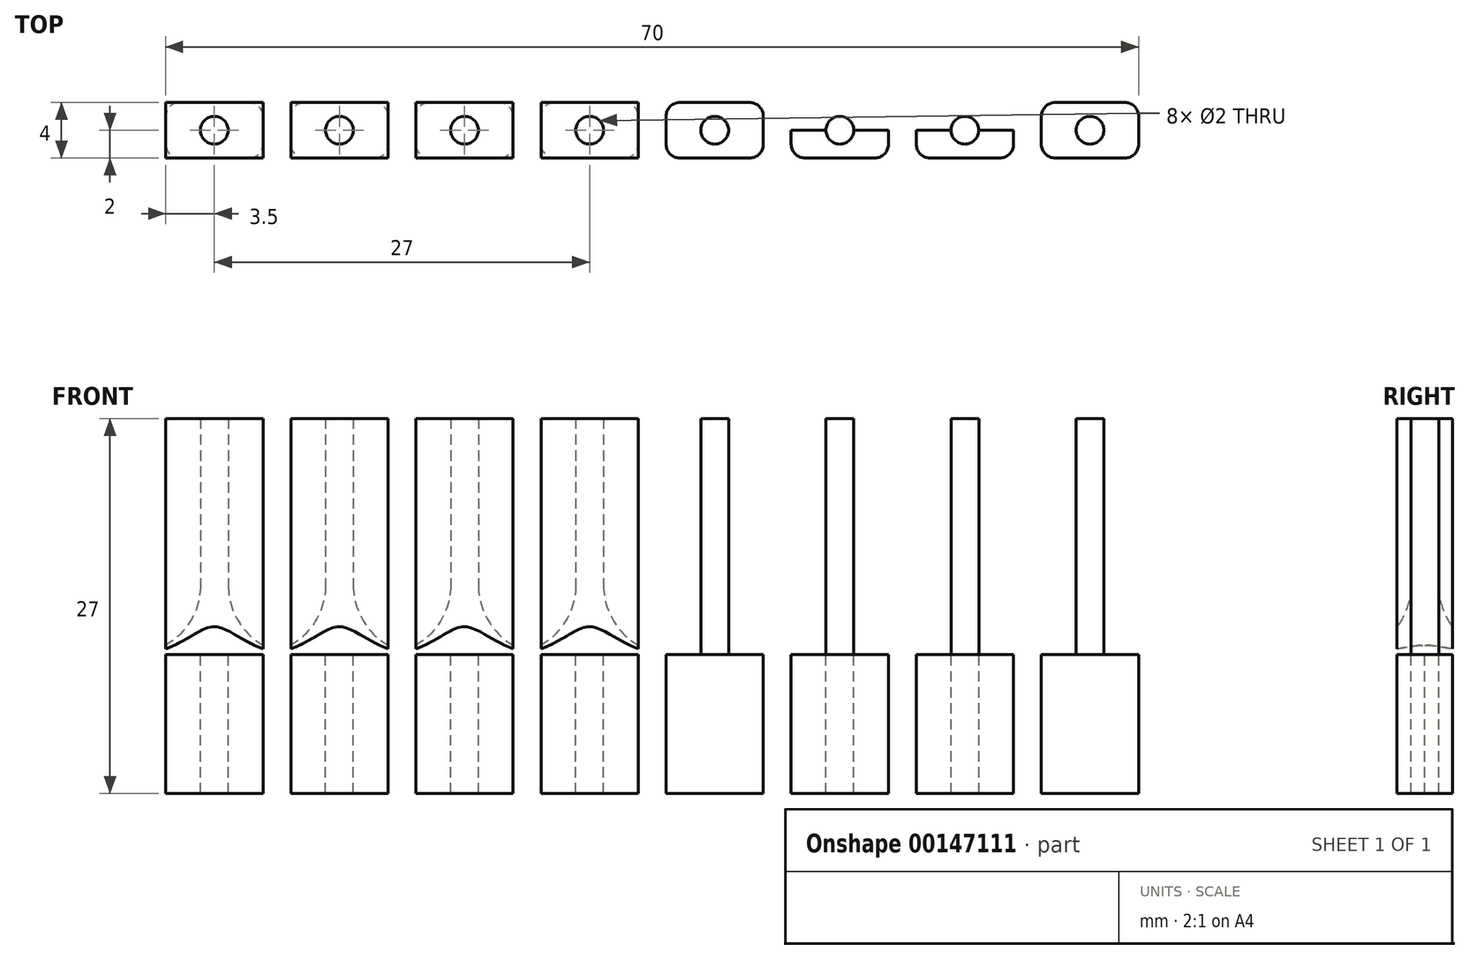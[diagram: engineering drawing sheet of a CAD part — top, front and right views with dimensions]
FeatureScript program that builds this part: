
annotation { "Feature Type Name" : "Feature", "Feature Type Description" : "" }
export const myFeature = defineFeature(function(context is Context, id is Id, definition is map)
    precondition{}
    {
        {
            var Q0;
            Q0=qCreatedBy(makeId("Top.planeOp"),FACE);
            var sketch = newSketch(context, id + "F0", { "sketchPlane" : qUnion([Q0])});
            skLineSegment(sketch, "E0.bottom", {"start": v(35, 2) * mm, "end": v(-35, 2) * mm});
            skLineSegment(sketch, "E0.top", {"start": v(35, -2) * mm, "end": v(-35, -2) * mm});
            skLineSegment(sketch, "E0.left", {"start": v(35, 2) * mm, "end": v(35, -2) * mm});
            skLineSegment(sketch, "E0.right", {"start": v(-35, 2) * mm, "end": v(-35, -2) * mm});
            skPoint(sketch, "E0.middle", {"position": v(0, 0) * mm});
            skLineSegment(sketch, "E1", {"start": v(0, 0) * mm, "end": v(4.5, 0) * mm});
            skLineSegment(sketch, "E2", {"start": v(4.5, 0) * mm, "end": v(13.5, 0) * mm});
            skLineSegment(sketch, "E3", {"start": v(13.5, 0) * mm, "end": v(22.5, 0) * mm});
            skLineSegment(sketch, "E4", {"start": v(22.5, 0) * mm, "end": v(31.5, 0) * mm});
            skCircle(sketch, "E5", {"center": v(4.5, 0) * mm, "radius": 1 * mm});
            skCircle(sketch, "E6", {"center": v(13.5, 0) * mm, "radius": 1 * mm});
            skCircle(sketch, "E7", {"center": v(22.5, 0) * mm, "radius": 1 * mm});
            skCircle(sketch, "E8", {"center": v(31.5, 0) * mm, "radius": 1 * mm});
            skLineSegment(sketch, "E9", {"start": v(0, 2) * mm, "end": v(8, 2) * mm});
            skLineSegment(sketch, "E10", {"start": v(8, 2) * mm, "end": v(10, 2) * mm});
            skLineSegment(sketch, "E11", {"start": v(10, 2) * mm, "end": v(17, 2) * mm});
            skLineSegment(sketch, "E12", {"start": v(17, 2) * mm, "end": v(19, 2) * mm});
            skLineSegment(sketch, "E13", {"start": v(19, 2) * mm, "end": v(26, 2) * mm});
            skLineSegment(sketch, "E14", {"start": v(26, 2) * mm, "end": v(28, 2) * mm});
            skLineSegment(sketch, "E15", {"start": v(8, 2) * mm, "end": v(8, 0.5) * mm});
            skLineSegment(sketch, "E16", {"start": v(8, 0.5) * mm, "end": v(10, 0.5) * mm});
            skLineSegment(sketch, "E17", {"start": v(10, 0.5) * mm, "end": v(10, 2) * mm});
            skLineSegment(sketch, "E18", {"start": v(17, 2) * mm, "end": v(17, 0.5) * mm});
            skLineSegment(sketch, "E19", {"start": v(17, 0.5) * mm, "end": v(19, 0.5) * mm});
            skLineSegment(sketch, "E20", {"start": v(19, 0.5) * mm, "end": v(19, 2) * mm});
            skLineSegment(sketch, "E21", {"start": v(26, 2) * mm, "end": v(26, 0.5) * mm});
            skLineSegment(sketch, "E22", {"start": v(26, 0.5) * mm, "end": v(28, 0.5) * mm});
            skLineSegment(sketch, "E23", {"start": v(28, 0.5) * mm, "end": v(28, 2) * mm});
            skLineSegment(sketch, "E24.MirrorCS", {"start": v(8, -0.5) * mm, "end": v(10, -0.5) * mm});
            skLineSegment(sketch, "E25.MirrorCS", {"start": v(8, -2) * mm, "end": v(8, -0.5) * mm});
            skLineSegment(sketch, "E26.MirrorCS", {"start": v(10, -0.5) * mm, "end": v(10, -2) * mm});
            skLineSegment(sketch, "E27.MirrorCS", {"start": v(17, -2) * mm, "end": v(17, -0.5) * mm});
            skLineSegment(sketch, "E28.MirrorCS", {"start": v(19, -0.5) * mm, "end": v(19, -2) * mm});
            skLineSegment(sketch, "E29.MirrorCS", {"start": v(17, -0.5) * mm, "end": v(19, -0.5) * mm});
            skLineSegment(sketch, "E30.MirrorCS", {"start": v(26, -0.5) * mm, "end": v(28, -0.5) * mm});
            skLineSegment(sketch, "E31.MirrorCS", {"start": v(28, -0.5) * mm, "end": v(28, -2) * mm});
            skLineSegment(sketch, "E32.MirrorCS", {"start": v(26, -2) * mm, "end": v(26, -0.5) * mm});
            skLineSegment(sketch, "E33", {"start": v(10, -0.5) * mm, "end": v(10, 0.5) * mm});
            skLineSegment(sketch, "E34", {"start": v(8, -0.5) * mm, "end": v(8, 0.5) * mm});
            skLineSegment(sketch, "E35", {"start": v(17, -0.5) * mm, "end": v(17, 0.5) * mm});
            skLineSegment(sketch, "E36", {"start": v(19, -0.5) * mm, "end": v(19, 0.5) * mm});
            skLineSegment(sketch, "E37", {"start": v(26, -0.5) * mm, "end": v(26, 0.5) * mm});
            skLineSegment(sketch, "E38", {"start": v(28, -0.5) * mm, "end": v(28, 0.5) * mm});
            skLineSegment(sketch, "E39.MirrorCS", {"start": v(-8, -2) * mm, "end": v(-8, -0.5) * mm});
            skCircle(sketch, "E40.MirrorC", {"center": v(-4.5, 0) * mm, "radius": 1 * mm});
            skLineSegment(sketch, "E41.MirrorCS", {"start": v(-8, 2) * mm, "end": v(-8, 0.5) * mm});
            skLineSegment(sketch, "E42.MirrorCS", {"start": v(-8, 0.5) * mm, "end": v(-10, 0.5) * mm});
            skLineSegment(sketch, "E43.MirrorCS", {"start": v(-10, -0.5) * mm, "end": v(-10, -2) * mm});
            skCircle(sketch, "E44.MirrorC", {"center": v(-13.5, 0) * mm, "radius": 1 * mm});
            skLineSegment(sketch, "E45.MirrorCS", {"start": v(-17, -2) * mm, "end": v(-17, -0.5) * mm});
            skLineSegment(sketch, "E46.MirrorCS", {"start": v(-19, -0.5) * mm, "end": v(-19, -2) * mm});
            skLineSegment(sketch, "E47.MirrorCS", {"start": v(-17, -0.5) * mm, "end": v(-19, -0.5) * mm});
            skLineSegment(sketch, "E48.MirrorCS", {"start": v(-17, 0.5) * mm, "end": v(-19, 0.5) * mm});
            skLineSegment(sketch, "E49.MirrorCS", {"start": v(-19, 0.5) * mm, "end": v(-19, 2) * mm});
            skLineSegment(sketch, "E50.MirrorCS", {"start": v(-17, 2) * mm, "end": v(-17, 0.5) * mm});
            skCircle(sketch, "E51.MirrorC", {"center": v(-22.5, 0) * mm, "radius": 1 * mm});
            skLineSegment(sketch, "E52.MirrorCS", {"start": v(-26, -2) * mm, "end": v(-26, -0.5) * mm});
            skLineSegment(sketch, "E53.MirrorCS", {"start": v(-28, -0.5) * mm, "end": v(-28, -2) * mm});
            skLineSegment(sketch, "E54.MirrorCS", {"start": v(-26, -0.5) * mm, "end": v(-28, -0.5) * mm});
            skLineSegment(sketch, "E55.MirrorCS", {"start": v(-26, 0.5) * mm, "end": v(-28, 0.5) * mm});
            skLineSegment(sketch, "E56.MirrorCS", {"start": v(-28, 0.5) * mm, "end": v(-28, 2) * mm});
            skLineSegment(sketch, "E57.MirrorCS", {"start": v(-26, 2) * mm, "end": v(-26, 0.5) * mm});
            skCircle(sketch, "E58.MirrorC", {"center": v(-31.5, 0) * mm, "radius": 1 * mm});
            skLineSegment(sketch, "E59.MirrorCS", {"start": v(-28, -0.5) * mm, "end": v(-28, 0.5) * mm});
            skLineSegment(sketch, "E60.MirrorCS", {"start": v(-26, -0.5) * mm, "end": v(-26, 0.5) * mm});
            skLineSegment(sketch, "E61.MirrorCS", {"start": v(-19, -0.5) * mm, "end": v(-19, 0.5) * mm});
            skLineSegment(sketch, "E62.MirrorCS", {"start": v(-17, -0.5) * mm, "end": v(-17, 0.5) * mm});
            skLineSegment(sketch, "E63.MirrorCS", {"start": v(-8, -0.5) * mm, "end": v(-8, 0.5) * mm});
            skLineSegment(sketch, "E64.MirrorCS", {"start": v(-10, -0.5) * mm, "end": v(-10, 0.5) * mm});
            skLineSegment(sketch, "E65.MirrorCS", {"start": v(-8, -0.5) * mm, "end": v(-10, -0.5) * mm});
            skLineSegment(sketch, "E66.MirrorCS", {"start": v(-10, 0.5) * mm, "end": v(-10, 2) * mm});
            skLineSegment(sketch, "E67", {"start": v(8, 2) * mm, "end": v(1, 2) * mm});
            skLineSegment(sketch, "E68", {"start": v(1, 2) * mm, "end": v(1, 0.5) * mm});
            skLineSegment(sketch, "E69", {"start": v(1, 0.5) * mm, "end": v(-1, 0.5) * mm});
            skLineSegment(sketch, "E70", {"start": v(-1, 0.5) * mm, "end": v(-1, 2) * mm});
            skLineSegment(sketch, "E71", {"start": v(8, -2) * mm, "end": v(1, -2) * mm});
            skLineSegment(sketch, "E72", {"start": v(1, -2) * mm, "end": v(1, -0.5) * mm});
            skLineSegment(sketch, "E73", {"start": v(1, -0.5) * mm, "end": v(-1, -0.5) * mm});
            skLineSegment(sketch, "E74", {"start": v(-1, -0.5) * mm, "end": v(-1, -2) * mm});
            skLineSegment(sketch, "E75", {"start": v(1, -0.5) * mm, "end": v(1, 0.5) * mm});
            skLineSegment(sketch, "E76", {"start": v(-1, -0.5) * mm, "end": v(-1, 0.5) * mm});
            skSolve(sketch);
        }
        {
            var Q0;
            {var subQ0=sQuery(id+"F0.wireOp",EDGE,"E0.left");Q0=makeQuery(id+"F0.imprint","IMPRINT",FACE,{"disambiguationData":[TD([[makeQuery(id+"F0.imprint","IMPRINT",EDGE,{"derivedFrom":subQ0}),-1.0]])]});}
            var Q1;
            {var subQ6=sQuery(id+"F0.wireOp",EDGE,"E0.right");Q1=makeQuery(id+"F0.imprint","IMPRINT",FACE,{"disambiguationData":[TD([[makeQuery(id+"F0.imprint","IMPRINT",EDGE,{"derivedFrom":subQ6}),1.0]])]});}
            var Q2;
            {var subQ10=sQuery(id+"F0.wireOp",EDGE,"E28.MirrorCS");Q2=makeQuery(id+"F0.imprint","IMPRINT",FACE,{"disambiguationData":[TD([[makeQuery(id+"F0.imprint","IMPRINT",EDGE,{"derivedFrom":subQ10}),1.0]])]});}
            var Q3;
            {var subQ5=sQuery(id+"F0.wireOp",EDGE,"E26.MirrorCS");Q3=makeQuery(id+"F0.imprint","IMPRINT",FACE,{"disambiguationData":[TD([[makeQuery(id+"F0.imprint","IMPRINT",EDGE,{"derivedFrom":subQ5}),1.0]])]});}
            var Q4;
            Q4=makeQuery(id+"F0.imprint","IMPRINT",FACE,{"disambiguationData":[TD([[makeQuery(id+"F0.imprint","IMPRINT",EDGE,{"derivedFrom":sQuery(id+"F0.wireOp",EDGE,"E11")}),-1.0]])]});
            var Q5;
            Q5=makeQuery(id+"F0.imprint","IMPRINT",FACE,{"disambiguationData":[TD([[makeQuery(id+"F0.imprint","IMPRINT",EDGE,{"derivedFrom":sQuery(id+"F0.wireOp",EDGE,"E13")}),-1.0]])]});
            var Q6;
            {var subQ1=sQuery(id+"F0.wireOp",EDGE,"E46.MirrorCS");Q6=makeQuery(id+"F0.imprint","IMPRINT",FACE,{"disambiguationData":[TD([[makeQuery(id+"F0.imprint","IMPRINT",EDGE,{"derivedFrom":subQ1}),-1.0]])]});}
            var Q7;
            {var subQ0=sQuery(id+"F0.wireOp",EDGE,"E43.MirrorCS");Q7=makeQuery(id+"F0.imprint","IMPRINT",FACE,{"disambiguationData":[TD([[makeQuery(id+"F0.imprint","IMPRINT",EDGE,{"derivedFrom":subQ0}),-1.0]])]});}
            var Q8;
            {var subQ2=sQuery(id+"F0.wireOp",EDGE,"E15");Q8=makeQuery(id+"F0.imprint","IMPRINT",FACE,{"disambiguationData":[TD([[makeQuery(id+"F0.imprint","IMPRINT",EDGE,{"derivedFrom":subQ2}),-1.0]])]});}
            var Q9;
            {var subQ0=sQuery(id+"F0.wireOp",EDGE,"E25.MirrorCS");Q9=makeQuery(id+"F0.imprint","IMPRINT",FACE,{"disambiguationData":[TD([[makeQuery(id+"F0.imprint","IMPRINT",EDGE,{"derivedFrom":subQ0}),1.0]])]});}
            var Q10;
            {var subQ0=sQuery(id+"F0.wireOp",EDGE,"E39.MirrorCS");Q10=makeQuery(id+"F0.imprint","IMPRINT",FACE,{"disambiguationData":[TD([[makeQuery(id+"F0.imprint","IMPRINT",EDGE,{"derivedFrom":subQ0}),-1.0]])]});}
            var Q11;
            Q11=makeQuery(id+"F0.imprint","IMPRINT",FACE,{"disambiguationData":[TD([[makeQuery(id+"F0.imprint","IMPRINT",EDGE,{"derivedFrom":sQuery(id+"F0.wireOp",EDGE,"E8")}),1.0]])]});
            var Q12;
            {var subQ0=sQuery(id+"F0.wireOp",EDGE,"E4");var subQ1=sQuery(id+"F0.wireOp",EDGE,"E3");var subQ2=makeQuery(id+"F0.imprint","INTERSECT",VERTEX,{"derivedFrom":[subQ1,subQ0]});Q12=makeQuery(id+"F0.imprint","IMPRINT",FACE,{"disambiguationData":[TD([[makeQuery(id+"F0.imprint","IMPRINT",EDGE,{"disambiguationData":[TD([[subQ2,1.0]])],"derivedFrom":subQ1}),1.0]])]});}
            var Q13;
            {var subQ0=sQuery(id+"F0.wireOp",EDGE,"E3");var subQ1=sQuery(id+"F0.wireOp",EDGE,"E2");var subQ2=makeQuery(id+"F0.imprint","INTERSECT",VERTEX,{"derivedFrom":[subQ1,subQ0]});Q13=makeQuery(id+"F0.imprint","IMPRINT",FACE,{"disambiguationData":[TD([[makeQuery(id+"F0.imprint","IMPRINT",EDGE,{"disambiguationData":[TD([[subQ2,1.0]])],"derivedFrom":subQ1}),1.0]])]});}
            var Q14;
            {var subQ0=sQuery(id+"F0.wireOp",EDGE,"E3");var subQ1=sQuery(id+"F0.wireOp",EDGE,"E2");var subQ2=makeQuery(id+"F0.imprint","INTERSECT",VERTEX,{"derivedFrom":[subQ1,subQ0]});Q14=makeQuery(id+"F0.imprint","IMPRINT",FACE,{"disambiguationData":[TD([[makeQuery(id+"F0.imprint","IMPRINT",EDGE,{"disambiguationData":[TD([[subQ2,1.0]])],"derivedFrom":subQ1}),-1.0]])]});}
            var Q15;
            {var subQ0=sQuery(id+"F0.wireOp",EDGE,"E4");var subQ1=sQuery(id+"F0.wireOp",EDGE,"E3");var subQ2=makeQuery(id+"F0.imprint","INTERSECT",VERTEX,{"derivedFrom":[subQ1,subQ0]});Q15=makeQuery(id+"F0.imprint","IMPRINT",FACE,{"disambiguationData":[TD([[makeQuery(id+"F0.imprint","IMPRINT",EDGE,{"disambiguationData":[TD([[subQ2,1.0]])],"derivedFrom":subQ1}),-1.0]])]});}
            var Q16;
            {var subQ0=sQuery(id+"F0.wireOp",EDGE,"E2");var subQ1=sQuery(id+"F0.wireOp",EDGE,"E1");var subQ2=makeQuery(id+"F0.imprint","INTERSECT",VERTEX,{"derivedFrom":[subQ1,subQ0]});Q16=makeQuery(id+"F0.imprint","IMPRINT",FACE,{"disambiguationData":[TD([[makeQuery(id+"F0.imprint","IMPRINT",EDGE,{"disambiguationData":[TD([[subQ2,1.0]])],"derivedFrom":subQ1}),1.0]])]});}
            var Q17;
            {var subQ0=sQuery(id+"F0.wireOp",EDGE,"E2");var subQ1=sQuery(id+"F0.wireOp",EDGE,"E1");var subQ2=makeQuery(id+"F0.imprint","INTERSECT",VERTEX,{"derivedFrom":[subQ1,subQ0]});Q17=makeQuery(id+"F0.imprint","IMPRINT",FACE,{"disambiguationData":[TD([[makeQuery(id+"F0.imprint","IMPRINT",EDGE,{"disambiguationData":[TD([[subQ2,1.0]])],"derivedFrom":subQ1}),-1.0]])]});}
            var Q18;
            Q18=makeQuery(id+"F0.imprint","IMPRINT",FACE,{"disambiguationData":[TD([[makeQuery(id+"F0.imprint","IMPRINT",EDGE,{"derivedFrom":sQuery(id+"F0.wireOp",EDGE,"E40.MirrorC")}),-1.0]])]});
            var Q19;
            Q19=makeQuery(id+"F0.imprint","IMPRINT",FACE,{"disambiguationData":[TD([[makeQuery(id+"F0.imprint","IMPRINT",EDGE,{"derivedFrom":sQuery(id+"F0.wireOp",EDGE,"E44.MirrorC")}),-1.0]])]});
            var Q20;
            Q20=makeQuery(id+"F0.imprint","IMPRINT",FACE,{"disambiguationData":[TD([[makeQuery(id+"F0.imprint","IMPRINT",EDGE,{"derivedFrom":sQuery(id+"F0.wireOp",EDGE,"E51.MirrorC")}),-1.0]])]});
            var Q21;
            Q21=makeQuery(id+"F0.imprint","IMPRINT",FACE,{"disambiguationData":[TD([[makeQuery(id+"F0.imprint","IMPRINT",EDGE,{"derivedFrom":sQuery(id+"F0.wireOp",EDGE,"E58.MirrorC")}),-1.0]])]});
            extrude(context, id + "F1", {"entities" : qUnion([Q0, Q1, Q2, Q3, Q4, Q5, Q6, Q7, Q8, Q9, Q10, Q11, Q12, Q13, Q14, Q15, Q16, Q17, Q18, Q19, Q20, Q21]), "oppositeDirection" : true, "depth" : 10 * mm});
        }
        {
            var Q0;
            {var subQ0=sQuery(id+"F0.wireOp",EDGE,"E2");var subQ1=sQuery(id+"F0.wireOp",EDGE,"E1");var subQ2=makeQuery(id+"F0.imprint","INTERSECT",VERTEX,{"derivedFrom":[subQ1,subQ0]});Q0=makeQuery(id+"F0.imprint","IMPRINT",FACE,{"disambiguationData":[TD([[makeQuery(id+"F0.imprint","IMPRINT",EDGE,{"disambiguationData":[TD([[subQ2,1.0]])],"derivedFrom":subQ1}),-1.0]])]});}
            var Q1;
            {var subQ0=sQuery(id+"F0.wireOp",EDGE,"E3");var subQ1=sQuery(id+"F0.wireOp",EDGE,"E2");var subQ2=makeQuery(id+"F0.imprint","INTERSECT",VERTEX,{"derivedFrom":[subQ1,subQ0]});Q1=makeQuery(id+"F0.imprint","IMPRINT",FACE,{"disambiguationData":[TD([[makeQuery(id+"F0.imprint","IMPRINT",EDGE,{"disambiguationData":[TD([[subQ2,1.0]])],"derivedFrom":subQ1}),-1.0]])]});}
            var Q2;
            {var subQ0=sQuery(id+"F0.wireOp",EDGE,"E4");var subQ1=sQuery(id+"F0.wireOp",EDGE,"E3");var subQ2=makeQuery(id+"F0.imprint","INTERSECT",VERTEX,{"derivedFrom":[subQ1,subQ0]});Q2=makeQuery(id+"F0.imprint","IMPRINT",FACE,{"disambiguationData":[TD([[makeQuery(id+"F0.imprint","IMPRINT",EDGE,{"disambiguationData":[TD([[subQ2,1.0]])],"derivedFrom":subQ1}),-1.0]])]});}
            var Q3;
            Q3=makeQuery(id+"F0.imprint","IMPRINT",FACE,{"disambiguationData":[TD([[makeQuery(id+"F0.imprint","IMPRINT",EDGE,{"derivedFrom":sQuery(id+"F0.wireOp",EDGE,"E8")}),1.0]])]});
            var Q4;
            {var subQ0=sQuery(id+"F0.wireOp",EDGE,"E4");var subQ1=sQuery(id+"F0.wireOp",EDGE,"E3");var subQ2=makeQuery(id+"F0.imprint","INTERSECT",VERTEX,{"derivedFrom":[subQ1,subQ0]});Q4=makeQuery(id+"F0.imprint","IMPRINT",FACE,{"disambiguationData":[TD([[makeQuery(id+"F0.imprint","IMPRINT",EDGE,{"disambiguationData":[TD([[subQ2,1.0]])],"derivedFrom":subQ1}),1.0]])]});}
            var Q5;
            {var subQ0=sQuery(id+"F0.wireOp",EDGE,"E3");var subQ1=sQuery(id+"F0.wireOp",EDGE,"E2");var subQ2=makeQuery(id+"F0.imprint","INTERSECT",VERTEX,{"derivedFrom":[subQ1,subQ0]});Q5=makeQuery(id+"F0.imprint","IMPRINT",FACE,{"disambiguationData":[TD([[makeQuery(id+"F0.imprint","IMPRINT",EDGE,{"disambiguationData":[TD([[subQ2,1.0]])],"derivedFrom":subQ1}),1.0]])]});}
            var Q6;
            {var subQ0=sQuery(id+"F0.wireOp",EDGE,"E2");var subQ1=sQuery(id+"F0.wireOp",EDGE,"E1");var subQ2=makeQuery(id+"F0.imprint","INTERSECT",VERTEX,{"derivedFrom":[subQ1,subQ0]});Q6=makeQuery(id+"F0.imprint","IMPRINT",FACE,{"disambiguationData":[TD([[makeQuery(id+"F0.imprint","IMPRINT",EDGE,{"disambiguationData":[TD([[subQ2,1.0]])],"derivedFrom":subQ1}),1.0]])]});}
            var Q7;
            Q7=makeQuery(id+"F0.imprint","IMPRINT",FACE,{"disambiguationData":[TD([[makeQuery(id+"F0.imprint","IMPRINT",EDGE,{"derivedFrom":sQuery(id+"F0.wireOp",EDGE,"E40.MirrorC")}),-1.0]])]});
            var Q8;
            Q8=makeQuery(id+"F0.imprint","IMPRINT",FACE,{"disambiguationData":[TD([[makeQuery(id+"F0.imprint","IMPRINT",EDGE,{"derivedFrom":sQuery(id+"F0.wireOp",EDGE,"E44.MirrorC")}),-1.0]])]});
            var Q9;
            Q9=makeQuery(id+"F0.imprint","IMPRINT",FACE,{"disambiguationData":[TD([[makeQuery(id+"F0.imprint","IMPRINT",EDGE,{"derivedFrom":sQuery(id+"F0.wireOp",EDGE,"E51.MirrorC")}),-1.0]])]});
            var Q10;
            Q10=makeQuery(id+"F0.imprint","IMPRINT",FACE,{"disambiguationData":[TD([[makeQuery(id+"F0.imprint","IMPRINT",EDGE,{"derivedFrom":sQuery(id+"F0.wireOp",EDGE,"E58.MirrorC")}),-1.0]])]});
            extrude(context, id + "F2", {"entities" : qUnion([Q0, Q1, Q2, Q3, Q4, Q5, Q6, Q7, Q8, Q9, Q10]), "depth" : 17 * mm});
        }
        {
            var Q0;
            Q0=makeQuery(id+"F1.opExtrude","SWEPT_EDGE",EDGE,{"disambiguationData":[OSD([sQuery(id+"F0.wireOp",EDGE,"E0.bottom"),sQuery(id+"F0.wireOp",EDGE,"E0.left")])]});
            var Q1;
            Q1=makeQuery(id+"F1.opExtrude","SWEPT_EDGE",EDGE,{"disambiguationData":[OSD([sQuery(id+"F0.wireOp",EDGE,"E0.bottom"),sQuery(id+"F0.wireOp",EDGE,"E14"),sQuery(id+"F0.wireOp",EDGE,"E23")])]});
            var Q2;
            Q2=makeQuery(id+"F1.opExtrude","SWEPT_EDGE",EDGE,{"disambiguationData":[OSD([sQuery(id+"F0.wireOp",EDGE,"E0.top"),sQuery(id+"F0.wireOp",EDGE,"E0.left")])]});
            var Q3;
            Q3=makeQuery(id+"F1.opExtrude","SWEPT_EDGE",EDGE,{"disambiguationData":[OSD([sQuery(id+"F0.wireOp",EDGE,"E13"),sQuery(id+"F0.wireOp",EDGE,"E14"),sQuery(id+"F0.wireOp",EDGE,"E21")])]});
            var Q4;
            Q4=makeQuery(id+"F1.opExtrude","SWEPT_EDGE",EDGE,{"disambiguationData":[OSD([sQuery(id+"F0.wireOp",EDGE,"E12"),sQuery(id+"F0.wireOp",EDGE,"E13"),sQuery(id+"F0.wireOp",EDGE,"E20")])]});
            var Q5;
            Q5=makeQuery(id+"F1.opExtrude","SWEPT_EDGE",EDGE,{"disambiguationData":[OSD([sQuery(id+"F0.wireOp",EDGE,"E11"),sQuery(id+"F0.wireOp",EDGE,"E12"),sQuery(id+"F0.wireOp",EDGE,"E18")])]});
            var Q6;
            Q6=makeQuery(id+"F1.opExtrude","SWEPT_EDGE",EDGE,{"disambiguationData":[OSD([sQuery(id+"F0.wireOp",EDGE,"E10"),sQuery(id+"F0.wireOp",EDGE,"E11"),sQuery(id+"F0.wireOp",EDGE,"E17")])]});
            var Q7;
            Q7=makeQuery(id+"F1.opExtrude","SWEPT_EDGE",EDGE,{"disambiguationData":[OSD([sQuery(id+"F0.wireOp",EDGE,"E10"),sQuery(id+"F0.wireOp",EDGE,"E15"),sQuery(id+"F0.wireOp",EDGE,"E67")])]});
            var Q8;
            Q8=makeQuery(id+"F1.opExtrude","SWEPT_EDGE",EDGE,{"disambiguationData":[OSD([sQuery(id+"F0.wireOp",EDGE,"E9"),sQuery(id+"F0.wireOp",EDGE,"E67"),sQuery(id+"F0.wireOp",EDGE,"E68")])]});
            var Q9;
            Q9=makeQuery(id+"F1.opExtrude","SWEPT_EDGE",EDGE,{"disambiguationData":[OSD([sQuery(id+"F0.wireOp",EDGE,"E0.bottom"),sQuery(id+"F0.wireOp",EDGE,"E70")])]});
            var Q10;
            Q10=makeQuery(id+"F1.opExtrude","SWEPT_EDGE",EDGE,{"disambiguationData":[OSD([sQuery(id+"F0.wireOp",EDGE,"E0.bottom"),sQuery(id+"F0.wireOp",EDGE,"E41.MirrorCS")])]});
            var Q11;
            Q11=makeQuery(id+"F1.opExtrude","SWEPT_EDGE",EDGE,{"disambiguationData":[OSD([sQuery(id+"F0.wireOp",EDGE,"E0.bottom"),sQuery(id+"F0.wireOp",EDGE,"E66.MirrorCS")])]});
            var Q12;
            Q12=makeQuery(id+"F1.opExtrude","SWEPT_EDGE",EDGE,{"disambiguationData":[OSD([sQuery(id+"F0.wireOp",EDGE,"E0.bottom"),sQuery(id+"F0.wireOp",EDGE,"E50.MirrorCS")])]});
            var Q13;
            Q13=makeQuery(id+"F1.opExtrude","SWEPT_EDGE",EDGE,{"disambiguationData":[OSD([sQuery(id+"F0.wireOp",EDGE,"E0.bottom"),sQuery(id+"F0.wireOp",EDGE,"E49.MirrorCS")])]});
            var Q14;
            Q14=makeQuery(id+"F1.opExtrude","SWEPT_EDGE",EDGE,{"disambiguationData":[OSD([sQuery(id+"F0.wireOp",EDGE,"E0.bottom"),sQuery(id+"F0.wireOp",EDGE,"E57.MirrorCS")])]});
            var Q15;
            Q15=makeQuery(id+"F1.opExtrude","SWEPT_EDGE",EDGE,{"disambiguationData":[OSD([sQuery(id+"F0.wireOp",EDGE,"E0.bottom"),sQuery(id+"F0.wireOp",EDGE,"E56.MirrorCS")])]});
            var Q16;
            Q16=makeQuery(id+"F1.opExtrude","SWEPT_EDGE",EDGE,{"disambiguationData":[OSD([sQuery(id+"F0.wireOp",EDGE,"E0.bottom"),sQuery(id+"F0.wireOp",EDGE,"E0.right")])]});
            var Q17;
            Q17=makeQuery(id+"F1.opExtrude","SWEPT_EDGE",EDGE,{"disambiguationData":[OSD([sQuery(id+"F0.wireOp",EDGE,"E0.top"),sQuery(id+"F0.wireOp",EDGE,"E31.MirrorCS")])]});
            var Q18;
            Q18=makeQuery(id+"F1.opExtrude","SWEPT_EDGE",EDGE,{"disambiguationData":[OSD([sQuery(id+"F0.wireOp",EDGE,"E0.top"),sQuery(id+"F0.wireOp",EDGE,"E32.MirrorCS")])]});
            var Q19;
            Q19=makeQuery(id+"F1.opExtrude","SWEPT_EDGE",EDGE,{"disambiguationData":[OSD([sQuery(id+"F0.wireOp",EDGE,"E0.top"),sQuery(id+"F0.wireOp",EDGE,"E28.MirrorCS")])]});
            var Q20;
            Q20=makeQuery(id+"F1.opExtrude","SWEPT_EDGE",EDGE,{"disambiguationData":[OSD([sQuery(id+"F0.wireOp",EDGE,"E0.top"),sQuery(id+"F0.wireOp",EDGE,"E27.MirrorCS")])]});
            var Q21;
            Q21=makeQuery(id+"F1.opExtrude","SWEPT_EDGE",EDGE,{"disambiguationData":[OSD([sQuery(id+"F0.wireOp",EDGE,"E0.top"),sQuery(id+"F0.wireOp",EDGE,"E26.MirrorCS")])]});
            var Q22;
            Q22=makeQuery(id+"F1.opExtrude","SWEPT_EDGE",EDGE,{"disambiguationData":[OSD([sQuery(id+"F0.wireOp",EDGE,"E0.top"),sQuery(id+"F0.wireOp",EDGE,"E25.MirrorCS"),sQuery(id+"F0.wireOp",EDGE,"E71")])]});
            var Q23;
            Q23=makeQuery(id+"F1.opExtrude","SWEPT_EDGE",EDGE,{"disambiguationData":[OSD([sQuery(id+"F0.wireOp",EDGE,"E0.top"),sQuery(id+"F0.wireOp",EDGE,"E71"),sQuery(id+"F0.wireOp",EDGE,"E72")])]});
            var Q24;
            Q24=makeQuery(id+"F1.opExtrude","SWEPT_EDGE",EDGE,{"disambiguationData":[OSD([sQuery(id+"F0.wireOp",EDGE,"E0.top"),sQuery(id+"F0.wireOp",EDGE,"E74")])]});
            var Q25;
            Q25=makeQuery(id+"F1.opExtrude","SWEPT_EDGE",EDGE,{"disambiguationData":[OSD([sQuery(id+"F0.wireOp",EDGE,"E0.top"),sQuery(id+"F0.wireOp",EDGE,"E39.MirrorCS")])]});
            var Q26;
            Q26=makeQuery(id+"F1.opExtrude","SWEPT_EDGE",EDGE,{"disambiguationData":[OSD([sQuery(id+"F0.wireOp",EDGE,"E0.top"),sQuery(id+"F0.wireOp",EDGE,"E43.MirrorCS")])]});
            var Q27;
            Q27=makeQuery(id+"F1.opExtrude","SWEPT_EDGE",EDGE,{"disambiguationData":[OSD([sQuery(id+"F0.wireOp",EDGE,"E0.top"),sQuery(id+"F0.wireOp",EDGE,"E45.MirrorCS")])]});
            var Q28;
            Q28=makeQuery(id+"F1.opExtrude","SWEPT_EDGE",EDGE,{"disambiguationData":[OSD([sQuery(id+"F0.wireOp",EDGE,"E0.top"),sQuery(id+"F0.wireOp",EDGE,"E46.MirrorCS")])]});
            var Q29;
            Q29=makeQuery(id+"F1.opExtrude","SWEPT_EDGE",EDGE,{"disambiguationData":[OSD([sQuery(id+"F0.wireOp",EDGE,"E0.top"),sQuery(id+"F0.wireOp",EDGE,"E52.MirrorCS")])]});
            var Q30;
            Q30=makeQuery(id+"F1.opExtrude","SWEPT_EDGE",EDGE,{"disambiguationData":[OSD([sQuery(id+"F0.wireOp",EDGE,"E0.top"),sQuery(id+"F0.wireOp",EDGE,"E53.MirrorCS")])]});
            var Q31;
            Q31=makeQuery(id+"F1.opExtrude","SWEPT_EDGE",EDGE,{"disambiguationData":[OSD([sQuery(id+"F0.wireOp",EDGE,"E0.top"),sQuery(id+"F0.wireOp",EDGE,"E0.right")])]});
            fillet(context, id + "F3", {"entities" : qUnion([Q0, Q1, Q2, Q3, Q4, Q5, Q6, Q7, Q8, Q9, Q10, Q11, Q12, Q13, Q14, Q15, Q16, Q17, Q18, Q19, Q20, Q21, Q22, Q23, Q24, Q25, Q26, Q27, Q28, Q29, Q30, Q31]), "radius" : 1 * mm, "tangentPropagation" : true, "allowEdgeOverflow" : false});
        }
        {
            var Q0;
            Q0=makeQuery(id+"F2.opExtrude","CAP_EDGE",EDGE,{"disambiguationData":[OSD([sQuery(id+"F0.wireOp",EDGE,"E58.MirrorC")])],"isStart":true});
            var Q1;
            Q1=makeQuery(id+"F2.opExtrude","CAP_EDGE",EDGE,{"disambiguationData":[OSD([sQuery(id+"F0.wireOp",EDGE,"E51.MirrorC")])],"isStart":true});
            var Q2;
            Q2=makeQuery(id+"F2.opExtrude","CAP_EDGE",EDGE,{"disambiguationData":[OSD([sQuery(id+"F0.wireOp",EDGE,"E44.MirrorC")])],"isStart":true});
            var Q3;
            Q3=makeQuery(id+"F2.opExtrude","CAP_EDGE",EDGE,{"disambiguationData":[OSD([sQuery(id+"F0.wireOp",EDGE,"E40.MirrorC")])],"isStart":true});
            var Q4;
            Q4=makeQuery(id+"F2.opExtrude","CAP_EDGE",EDGE,{"disambiguationData":[OSD([sQuery(id+"F0.wireOp",EDGE,"E5")])],"isStart":true});
            var Q5;
            Q5=makeQuery(id+"F2.opExtrude","CAP_EDGE",EDGE,{"disambiguationData":[OSD([sQuery(id+"F0.wireOp",EDGE,"E6")])],"isStart":true});
            var Q6;
            Q6=makeQuery(id+"F2.opExtrude","CAP_EDGE",EDGE,{"disambiguationData":[OSD([sQuery(id+"F0.wireOp",EDGE,"E7")])],"isStart":true});
            var Q7;
            Q7=makeQuery(id+"F2.opExtrude","CAP_EDGE",EDGE,{"disambiguationData":[OSD([sQuery(id+"F0.wireOp",EDGE,"E8")])],"isStart":true});
            fillet(context, id + "F4", {"entities" : qUnion([Q0, Q1, Q2, Q3, Q4, Q5, Q6, Q7]), "radius" : 5 * mm, "tangentPropagation" : true, "allowEdgeOverflow" : false});
        }
    });
